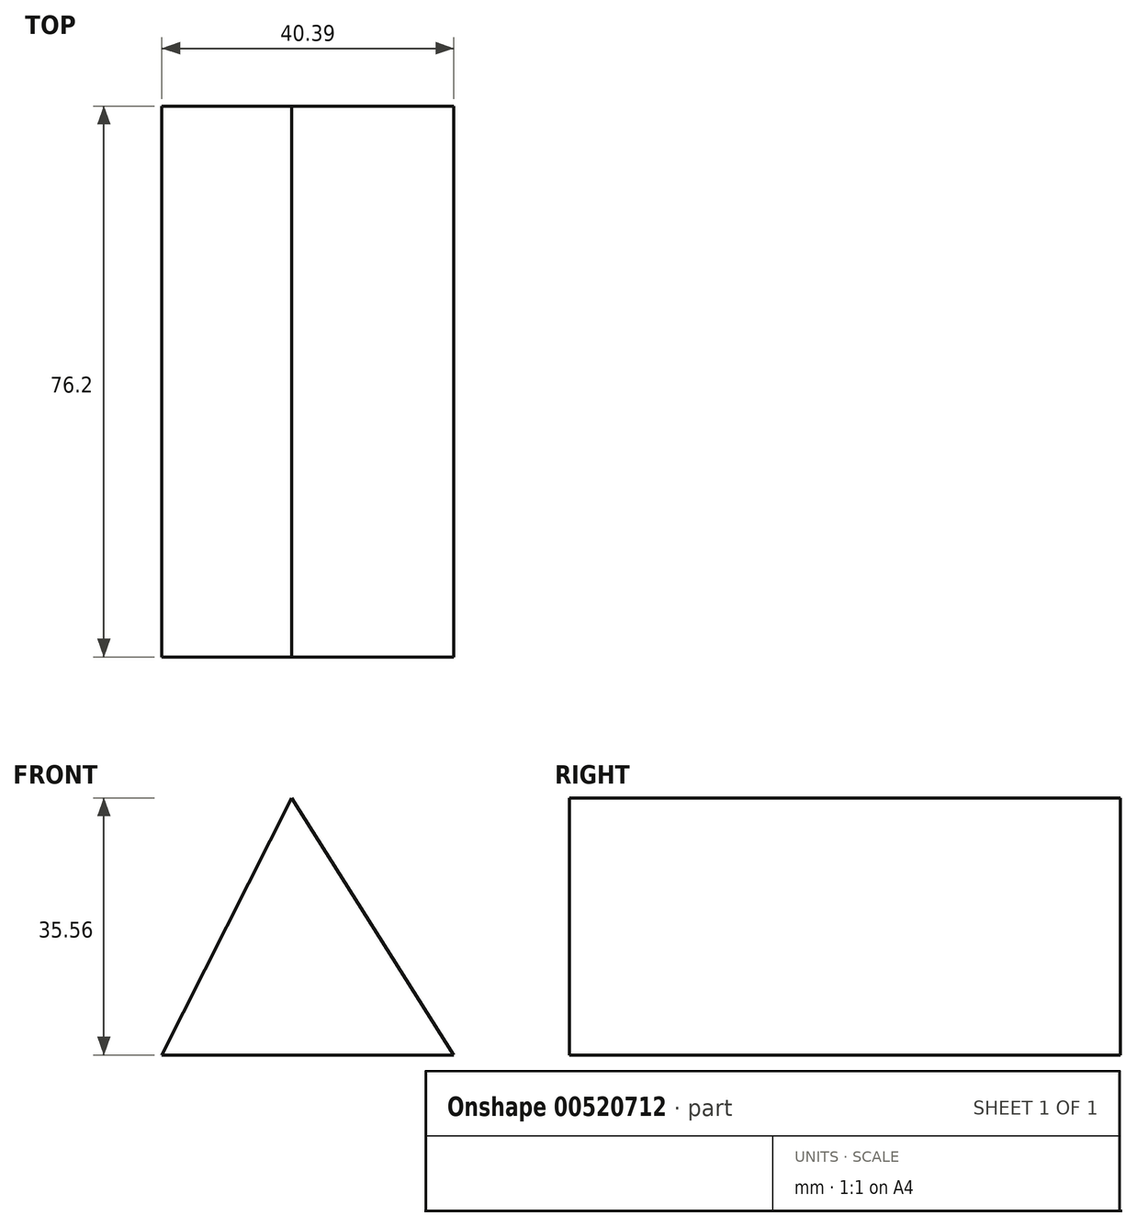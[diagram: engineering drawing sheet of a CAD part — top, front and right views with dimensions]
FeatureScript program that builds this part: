
annotation { "Feature Type Name" : "Feature", "Feature Type Description" : "" }
export const myFeature = defineFeature(function(context is Context, id is Id, definition is map)
    precondition{}
    {
        {
            var Q0;
            Q0=qCreatedBy(makeId("Front.planeOp"),FACE);
            var sketch = newSketch(context, id + "F0", { "sketchPlane" : qUnion([Q0])});
            skLineSegment(sketch, "E0", {"start": v(-32.42, 47) * mm, "end": v(-50.4, 11.43) * mm});
            skLineSegment(sketch, "E1", {"start": v(-32.42, 47) * mm, "end": v(-10.01, 11.43) * mm});
            skLineSegment(sketch, "E2", {"start": v(-10.01, 11.43) * mm, "end": v(-50.4, 11.43) * mm});
            skLineSegment(sketch, "E3", {"start": v(-32.42, 47) * mm, "end": v(-32.42, 11.43) * mm});
            skSolve(sketch);
        }
        {
            var Q0;
            Q0 = qSketchRegion(id + "F0", true);
            extrude(context, id + "F1", {"entities" : qUnion([Q0]), "depth" : 76.2 * mm, "offsetDistance" : 25.4 * mm});
        }
    });
